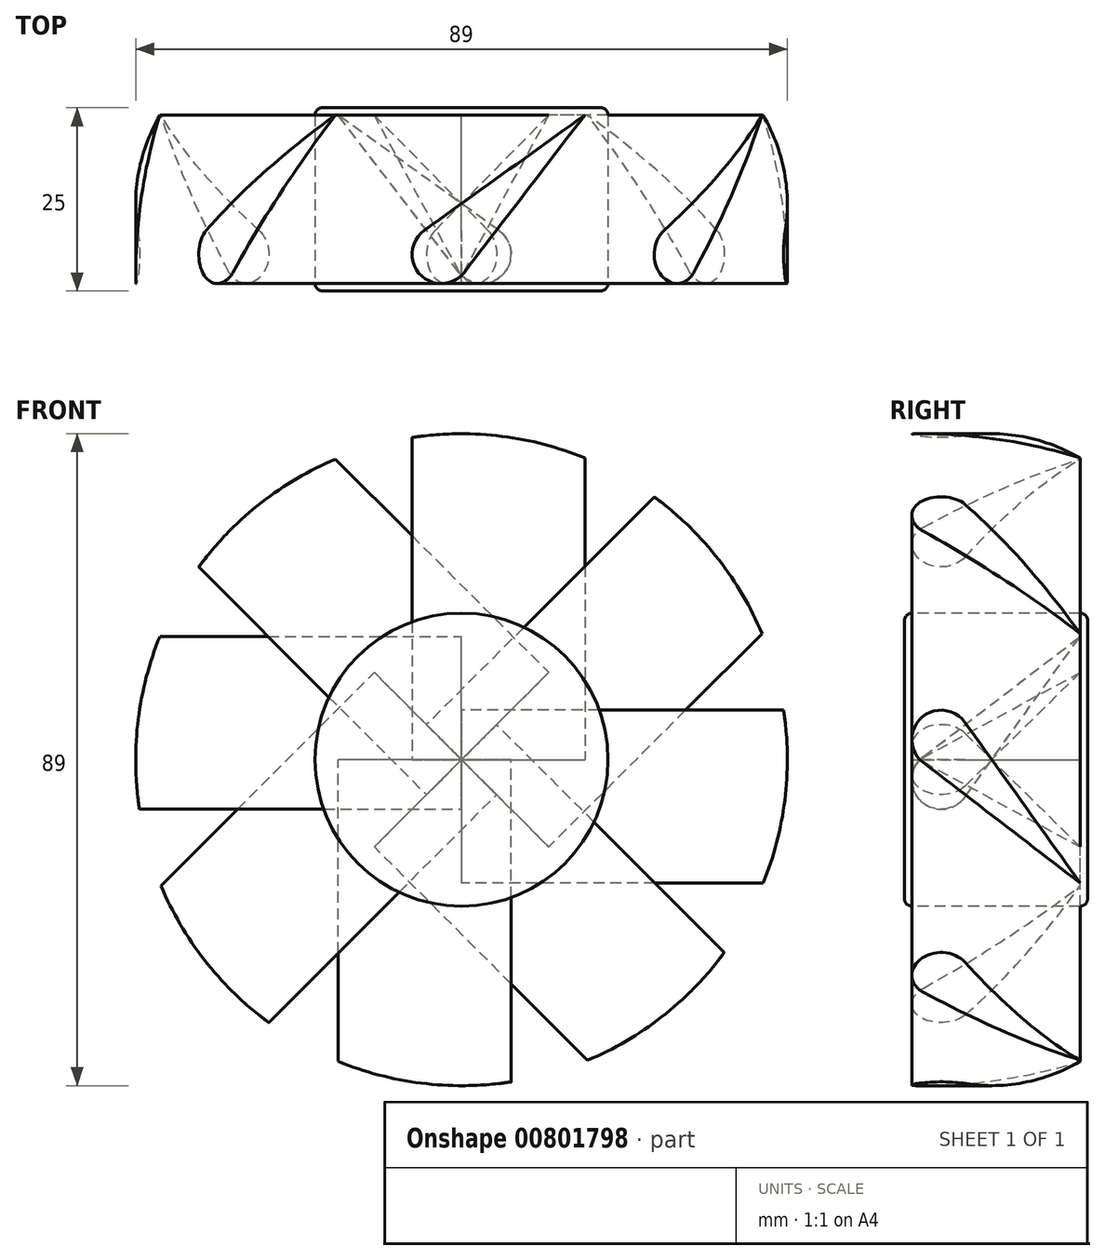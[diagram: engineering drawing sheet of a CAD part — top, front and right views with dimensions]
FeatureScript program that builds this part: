
annotation { "Feature Type Name" : "Feature", "Feature Type Description" : "" }
export const myFeature = defineFeature(function(context is Context, id is Id, definition is map)
    precondition{}
    {
        {
            var Q0;
            Q0=qCreatedBy(makeId("Front.planeOp"),FACE);
            var sketch = newSketch(context, id + "F0", { "sketchPlane" : qUnion([Q0])});
            skCircle(sketch, "E0", {"center": v(0, 0) * mm, "radius": 45 * mm});
            skLineSegment(sketch, "E1.bottom", {"start": v(46, -46) * mm, "end": v(-46, -46) * mm});
            skLineSegment(sketch, "E1.top", {"start": v(46, 46) * mm, "end": v(-46, 46) * mm});
            skLineSegment(sketch, "E1.left", {"start": v(46, -46) * mm, "end": v(46, 46) * mm});
            skLineSegment(sketch, "E1.right", {"start": v(-46, -46) * mm, "end": v(-46, 46) * mm});
            skLineSegment(sketch, "E2.bottom", {"start": v(41.25, -41.25) * mm, "end": v(-41.25, -41.25) * mm, "construction": true});
            skLineSegment(sketch, "E2.top", {"start": v(41.25, 41.25) * mm, "end": v(-41.25, 41.25) * mm, "construction": true});
            skLineSegment(sketch, "E2.left", {"start": v(41.25, -41.25) * mm, "end": v(41.25, 41.25) * mm, "construction": true});
            skLineSegment(sketch, "E2.right", {"start": v(-41.25, -41.25) * mm, "end": v(-41.25, 41.25) * mm, "construction": true});
            skCircle(sketch, "E3", {"center": v(-41.25, 41.25) * mm, "radius": 1.5 * mm});
            skCircle(sketch, "E4", {"center": v(41.25, 41.25) * mm, "radius": 1.5 * mm});
            skCircle(sketch, "E5", {"center": v(41.25, -41.25) * mm, "radius": 1.5 * mm});
            skCircle(sketch, "E6", {"center": v(-41.25, -41.25) * mm, "radius": 1.5 * mm});
            skSolve(sketch);
        }
        {
            var Q0;
            Q0=makeQuery(id+"F0.imprint","IMPRINT",FACE,{"disambiguationData":[TD([[makeQuery(id+"F0.imprint","IMPRINT",EDGE,{"derivedFrom":sQuery(id+"F0.wireOp",EDGE,"E0")}),-1.0]])]});
            extrude(context, id + "F1", {"entities" : qUnion([Q0]), "oppositeDirection" : true, "depth" : 25 * mm, "offsetDistance" : 25 * mm});
        }
        {
            var Q0;
            Q0=qCreatedBy(makeId("Right.planeOp"),FACE);
            var sketch = newSketch(context, id + "F2", { "sketchPlane" : qUnion([Q0])});
            skLineSegment(sketch, "E7", {"start": v(0, 0) * mm, "end": v(-17.7, 0) * mm, "construction": true});
            skPoint(sketch, "E8.0", {"position": v(0, 0) * mm});
            skCircle(sketch, "E9", {"center": v(5, 2.77) * mm, "radius": 4 * mm, "construction": true});
            skLineSegment(sketch, "E10", {"start": v(5, 2.77) * mm, "end": v(24, -16.84) * mm});
            skLineSegment(sketch, "E11", {"start": v(2.57, -0.4) * mm, "end": v(24, -16.84) * mm});
            skLineSegment(sketch, "E12", {"start": v(8.25, 5.1) * mm, "end": v(24, -16.84) * mm});
            skArc(sketch, "E13", {"start": v(2.57, -0.4) * mm, "mid": v(2.22, 5.64) * mm, "end": v(8.25, 5.1) * mm});
            skLineSegment(sketch, "E14.0", {"start": v(25, -46) * mm, "end": v(25, 46) * mm, "construction": true});
            skLineSegment(sketch, "E15", {"start": v(0, -4.63) * mm, "end": v(0, 9) * mm});
            skLineSegment(sketch, "E16", {"start": v(1, 2.77) * mm, "end": v(0, 2.77) * mm, "construction": true});
            skSolve(sketch);
        }
        {
            var Q0;
            Q0=qSketchRegion(id+"F2",true);
            extrude(context, id + "F3", {"entities" : qUnion([Q0]), "depth" : 50 * mm, "offsetDistance" : 25 * mm});
        }
        {
            var Q0;
            Q0=makeQuery(id+"F3.opExtrude","SWEPT_BODY",BODY,{"disambiguationData":[OSD([sQuery(id+"F2.wireOp",EDGE,"E11"),sQuery(id+"F2.wireOp",EDGE,"E12"),sQuery(id+"F2.wireOp",EDGE,"E13")])]});
            var Q1;
            Q1=sQuery(id+"F2.wireOp",EDGE,"E7");
            circularPattern(context, id + "F4", {"entities" : qUnion([Q0]), "axis" : qUnion([Q1]), "angle" : 360 * degree, "instanceCount" : 8, "equalSpace" : true});
        }
        {
            var Q0;
            Q0=qCreatedBy(makeId("Front.planeOp"),FACE);
            var sketch = newSketch(context, id + "F5", { "sketchPlane" : qUnion([Q0])});
            skCircle(sketch, "E17", {"center": v(0, 0) * mm, "radius": 20 * mm});
            skSolve(sketch);
        }
        {
            var Q0;
            Q0=qSketchRegion(id+"F5",true);
            extrude(context, id + "F6", {"entities" : qUnion([Q0]), "oppositeDirection" : true, "depth" : 25 * mm, "offsetDistance" : 25 * mm});
        }
        {
            var Q0;
            Q0=qCreatedBy(makeId("Front.planeOp"),FACE);
            var sketch = newSketch(context, id + "F7", { "sketchPlane" : qUnion([Q0])});
            skPoint(sketch, "E18.0", {"position": v(0, 0) * mm});
            skCircle(sketch, "E19", {"center": v(0, 0) * mm, "radius": 44.5 * mm});
            skLineSegment(sketch, "E20.bottom", {"start": v(60, -60) * mm, "end": v(-60, -60) * mm});
            skLineSegment(sketch, "E20.top", {"start": v(60, 60) * mm, "end": v(-60, 60) * mm});
            skLineSegment(sketch, "E20.left", {"start": v(60, -60) * mm, "end": v(60, 60) * mm});
            skLineSegment(sketch, "E20.right", {"start": v(-60, -60) * mm, "end": v(-60, 60) * mm});
            skSolve(sketch);
        }
        {
            var Q0;
            Q0 = qSketchRegion(id + "F7", true);
            extrude(context, id + "F8", {"entities" : qUnion([Q0]), "operationType" : NewBodyOperationType.REMOVE, "endBound" : BoundingType.THROUGH_ALL, "oppositeDirection" : true, "depth" : 25 * mm, "offsetDistance" : 25 * mm});
        }
        {
            var Q0;
            Q0=makeQuery(id+"F6.opExtrude","CAP_EDGE",EDGE,{"disambiguationData":[OSD([sQuery(id+"F5.wireOp",EDGE,"E17")])],"isStart":true});
            var Q1;
            Q1=makeQuery(id+"F6.opExtrude","CAP_EDGE",EDGE,{"disambiguationData":[OSD([sQuery(id+"F5.wireOp",EDGE,"E17")])],"isStart":false});
            fillet(context, id + "F9", {"entities" : qUnion([Q0, Q1]), "radius" : 1 * mm, "tangentPropagation" : true, "allowEdgeOverflow" : false});
        }
    });
